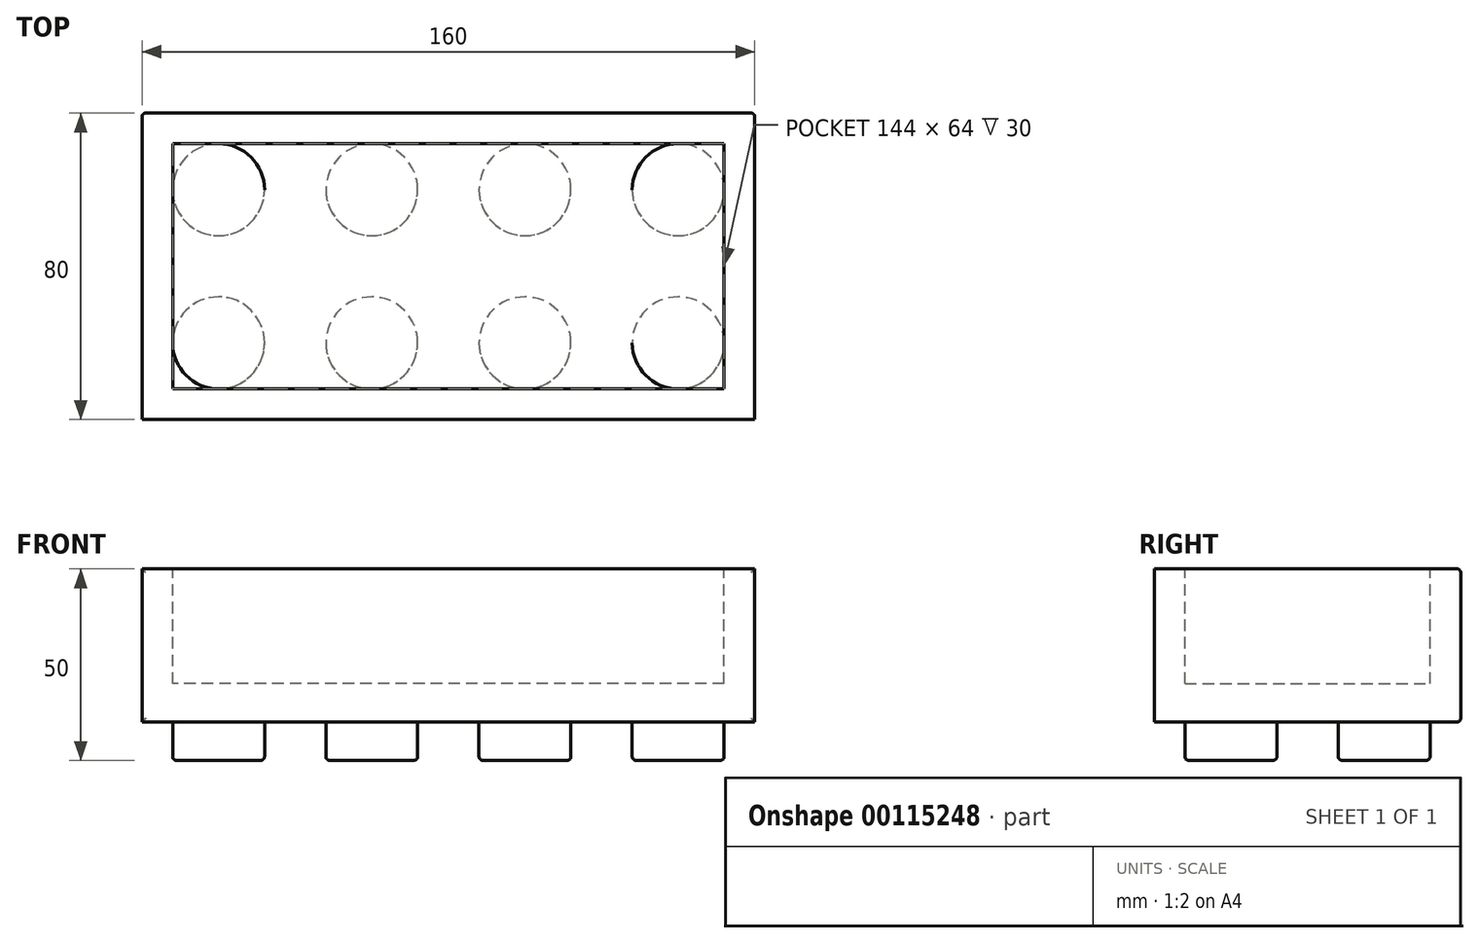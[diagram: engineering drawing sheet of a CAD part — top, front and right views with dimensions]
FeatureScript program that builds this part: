
annotation { "Feature Type Name" : "Feature", "Feature Type Description" : "" }
export const myFeature = defineFeature(function(context is Context, id is Id, definition is map)
    precondition{}
    {
        {
            var Q0;
            Q0=qCreatedBy(makeId("Top.planeOp"),FACE);
            var sketch = newSketch(context, id + "F0", { "sketchPlane" : qUnion([Q0])});
            skLineSegment(sketch, "E0.bottom", {"start": v(-77.45, 41.5) * mm, "end": v(82.55, 41.5) * mm});
            skLineSegment(sketch, "E0.top", {"start": v(-77.45, -38.5) * mm, "end": v(82.55, -38.5) * mm});
            skLineSegment(sketch, "E0.left", {"start": v(-77.45, 41.5) * mm, "end": v(-77.45, -38.5) * mm});
            skLineSegment(sketch, "E0.right", {"start": v(82.55, 41.5) * mm, "end": v(82.55, -38.5) * mm});
            skSolve(sketch);
        }
        {
            var Q0;
            Q0=makeQuery(id+"F0.imprint","IMPRINT",FACE,{"disambiguationData":[TD([[makeQuery(id+"F0.imprint","IMPRINT",EDGE,{"derivedFrom":sQuery(id+"F0.wireOp",EDGE,"E0.bottom")}),-1.0]])]});
            extrude(context, id + "F1", {"entities" : qUnion([Q0]), "depth" : 40 * mm});
        }
        {
            var Q0;
            Q0=makeQuery(id+"F1.opExtrude","CAP_FACE",FACE,{"disambiguationData":[OSD([sQuery(id+"F0.wireOp",EDGE,"E0.bottom"),sQuery(id+"F0.wireOp",EDGE,"E0.top"),sQuery(id+"F0.wireOp",EDGE,"E0.left"),sQuery(id+"F0.wireOp",EDGE,"E0.right")])],"isStart":false});
            var sketch = newSketch(context, id + "F2", { "sketchPlane" : qUnion([Q0])});
            skLineSegment(sketch, "E1.0", {"start": v(74.55, 33.5) * mm, "end": v(-69.45, 33.5) * mm});
            skLineSegment(sketch, "E1.1", {"start": v(74.55, -30.5) * mm, "end": v(74.55, 33.5) * mm});
            skLineSegment(sketch, "E1.2", {"start": v(-69.45, -30.5) * mm, "end": v(74.55, -30.5) * mm});
            skLineSegment(sketch, "E1.3", {"start": v(-69.45, 33.5) * mm, "end": v(-69.45, -30.5) * mm});
            skSolve(sketch);
        }
        {
            var Q0;
            Q0=makeQuery(id+"F2.imprint","IMPRINT",FACE,{"disambiguationData":[TD([[makeQuery(id+"F2.imprint","IMPRINT",EDGE,{"derivedFrom":sQuery(id+"F2.wireOp",EDGE,"E1.0")}),1.0]])]});
            extrude(context, id + "F3", {"entities" : qUnion([Q0]), "operationType" : NewBodyOperationType.REMOVE, "oppositeDirection" : true, "depth" : 30 * mm});
        }
        {
            var Q0;
            Q0=makeQuery(id+"F1.opExtrude","CAP_FACE",FACE,{"disambiguationData":[OSD([sQuery(id+"F0.wireOp",EDGE,"E0.bottom"),sQuery(id+"F0.wireOp",EDGE,"E0.top"),sQuery(id+"F0.wireOp",EDGE,"E0.left"),sQuery(id+"F0.wireOp",EDGE,"E0.right")])],"isStart":true});
            var sketch = newSketch(context, id + "F4", { "sketchPlane" : qUnion([Q0])});
            skCircle(sketch, "E2", {"center": v(-57.45, 18.5) * mm, "radius": 12 * mm});
            skCircle(sketch, "E3.0.1.0", {"center": v(-57.45, -21.5) * mm, "radius": 12 * mm});
            skCircle(sketch, "E3.1.0.0", {"center": v(-17.45, 18.5) * mm, "radius": 12 * mm});
            skCircle(sketch, "E3.1.1.0", {"center": v(-17.45, -21.5) * mm, "radius": 12 * mm});
            skCircle(sketch, "E3.2.0.0", {"center": v(22.55, 18.5) * mm, "radius": 12 * mm});
            skCircle(sketch, "E3.2.1.0", {"center": v(22.55, -21.5) * mm, "radius": 12 * mm});
            skCircle(sketch, "E3.3.0.0", {"center": v(62.55, 18.5) * mm, "radius": 12 * mm});
            skCircle(sketch, "E3.3.1.0", {"center": v(62.55, -21.5) * mm, "radius": 12 * mm});
            skLineSegment(sketch, "E3.direction1", {"start": v(-57.45, 18.5) * mm, "end": v(-17.45, 18.5) * mm, "construction": true});
            skLineSegment(sketch, "E3.direction2", {"start": v(-57.45, 18.5) * mm, "end": v(-57.45, -21.5) * mm, "construction": true});
            skSolve(sketch);
        }
        {
            var Q0;
            Q0=makeQuery(id+"F4.imprint","IMPRINT",FACE,{"disambiguationData":[TD([[makeQuery(id+"F4.imprint","IMPRINT",EDGE,{"derivedFrom":sQuery(id+"F4.wireOp",EDGE,"E2")}),1.0]])]});
            var Q1;
            Q1=makeQuery(id+"F4.imprint","IMPRINT",FACE,{"disambiguationData":[TD([[makeQuery(id+"F4.imprint","IMPRINT",EDGE,{"derivedFrom":sQuery(id+"F4.wireOp",EDGE,"E3.1.0.0")}),1.0]])]});
            var Q2;
            Q2=makeQuery(id+"F4.imprint","IMPRINT",FACE,{"disambiguationData":[TD([[makeQuery(id+"F4.imprint","IMPRINT",EDGE,{"derivedFrom":sQuery(id+"F4.wireOp",EDGE,"E3.2.0.0")}),1.0]])]});
            var Q3;
            Q3=makeQuery(id+"F4.imprint","IMPRINT",FACE,{"disambiguationData":[TD([[makeQuery(id+"F4.imprint","IMPRINT",EDGE,{"derivedFrom":sQuery(id+"F4.wireOp",EDGE,"E3.3.0.0")}),1.0]])]});
            var Q4;
            Q4=makeQuery(id+"F4.imprint","IMPRINT",FACE,{"disambiguationData":[TD([[makeQuery(id+"F4.imprint","IMPRINT",EDGE,{"derivedFrom":sQuery(id+"F4.wireOp",EDGE,"E3.3.1.0")}),1.0]])]});
            var Q5;
            Q5=makeQuery(id+"F4.imprint","IMPRINT",FACE,{"disambiguationData":[TD([[makeQuery(id+"F4.imprint","IMPRINT",EDGE,{"derivedFrom":sQuery(id+"F4.wireOp",EDGE,"E3.2.1.0")}),1.0]])]});
            var Q6;
            Q6=makeQuery(id+"F4.imprint","IMPRINT",FACE,{"disambiguationData":[TD([[makeQuery(id+"F4.imprint","IMPRINT",EDGE,{"derivedFrom":sQuery(id+"F4.wireOp",EDGE,"E3.1.1.0")}),1.0]])]});
            var Q7;
            Q7=makeQuery(id+"F4.imprint","IMPRINT",FACE,{"disambiguationData":[TD([[makeQuery(id+"F4.imprint","IMPRINT",EDGE,{"derivedFrom":sQuery(id+"F4.wireOp",EDGE,"E3.0.1.0")}),1.0]])]});
            extrude(context, id + "F5", {"entities" : qUnion([Q0, Q1, Q2, Q3, Q4, Q5, Q6, Q7]), "operationType" : NewBodyOperationType.ADD, "depth" : 10 * mm});
        }
        {
            var Q0;
            Q0=makeQuery(id+"F1.opExtrude","SWEPT_FACE",FACE,{"disambiguationData":[OSD([sQuery(id+"F0.wireOp",EDGE,"E0.bottom")])]});
            var Q1;
            Q1=makeQuery(id+"F5.opExtrude","CAP_FACE",FACE,{"disambiguationData":[OSD([sQuery(id+"F4.wireOp",EDGE,"E3.1.0.0")])],"isStart":false});
            var Q2;
            Q2=makeQuery(id+"F5.opExtrude","CAP_FACE",FACE,{"disambiguationData":[OSD([sQuery(id+"F4.wireOp",EDGE,"E3.2.0.0")])],"isStart":false});
            var Q3;
            Q3=makeQuery(id+"F5.opExtrude","CAP_FACE",FACE,{"disambiguationData":[OSD([sQuery(id+"F4.wireOp",EDGE,"E3.3.0.0")])],"isStart":false});
            var Q4;
            Q4=makeQuery(id+"F5.opExtrude","CAP_FACE",FACE,{"disambiguationData":[OSD([sQuery(id+"F4.wireOp",EDGE,"E3.3.1.0")])],"isStart":false});
            var Q5;
            Q5=makeQuery(id+"F5.opExtrude","CAP_FACE",FACE,{"disambiguationData":[OSD([sQuery(id+"F4.wireOp",EDGE,"E3.2.1.0")])],"isStart":false});
            var Q6;
            Q6=makeQuery(id+"F5.opExtrude","CAP_FACE",FACE,{"disambiguationData":[OSD([sQuery(id+"F4.wireOp",EDGE,"E3.1.1.0")])],"isStart":false});
            var Q7;
            Q7=makeQuery(id+"F5.opExtrude","CAP_FACE",FACE,{"disambiguationData":[OSD([sQuery(id+"F4.wireOp",EDGE,"E3.0.1.0")])],"isStart":false});
            var Q8;
            Q8=makeQuery(id+"F5.opExtrude","CAP_FACE",FACE,{"disambiguationData":[OSD([sQuery(id+"F4.wireOp",EDGE,"E2")])],"isStart":false});
            fillet(context, id + "F6", {"entities" : qUnion([Q0, Q1, Q2, Q3, Q4, Q5, Q6, Q7, Q8]), "radius" : 1 * mm, "tangentPropagation" : true, "allowEdgeOverflow" : false});
        }
    });
